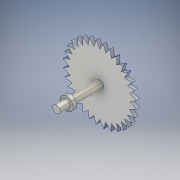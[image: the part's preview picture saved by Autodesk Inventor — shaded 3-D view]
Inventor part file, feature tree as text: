
AUTODESK INVENTOR PART (.ipt)
format: ipt  version: 2018 (Build 220112000, 112)  size: 260,608 bytes
history: native  units: in
note: dims shown in document units (in); Inventor stores cm internally (conversion verified against a paired STEP export)
features: sketch x8, extrude x7
ambient origin geometry x8: Origin, YZ Plane, XZ Plane, XY Plane, X Axis, Y Axis, Z Axis, Center Point
bodies: Solid1 (feature_tree)
feature tree (15):
  extrude  "Extrusion1"  Depth=0.103in TaperAngle=0.0deg
  extrude  "Extrusion2"  Depth=0.038in TaperAngle=0.0deg
  extrude  "Extrusion3"  Depth=0.306in
  extrude  "Extrusion4"  Depth=0.033in
  extrude  "Extrusion5"  Depth=0.064in
  extrude  "Extrusion6"  Depth=0.064in
  sketch  "Sketch8"  dims[d16=0.064in d17=0.064in]
  extrude  "Extrusion7"  Depth=0.064in
  sketch  "Sketch1"  dims[d0=0.077in d1=0.103in d2=0.0in]
  sketch  "Sketch2"  dims[d3=0.136in d4=0.038in d5=0.0in]
  sketch  "Sketch3"  dims[d6=0.306in d7=0.0in d8=0.63in]
  sketch  "Sketch4"  dims[d9=0.033in d10=0.0in d11=0.064in]
  sketch  "Sketch5"  dims[d12=0.064in d13=0.064in]
  sketch  "Sketch6"  dims[d14=0.064in d15=0.064in]
  sketch  "Sketch9"  dims[d18=0.064in d19=0.064in d20=0.064in d21=0.064in d22=0.064in d23=0.064in d24=0.064in d25=0.064in d26=0.064in d27=0.064in d28=0.064in d29=0.064in d30=0.064in d32=0.064in d33=0.064in d34=0.064in d35=0.064in d36=0.064in d37=0.064in d39=0.198in d40=0.112in d41=0.0in d42=0.077in d43=0.098in d44=0.0in d71=0.762in d72=0.033in d73=0.0in]
